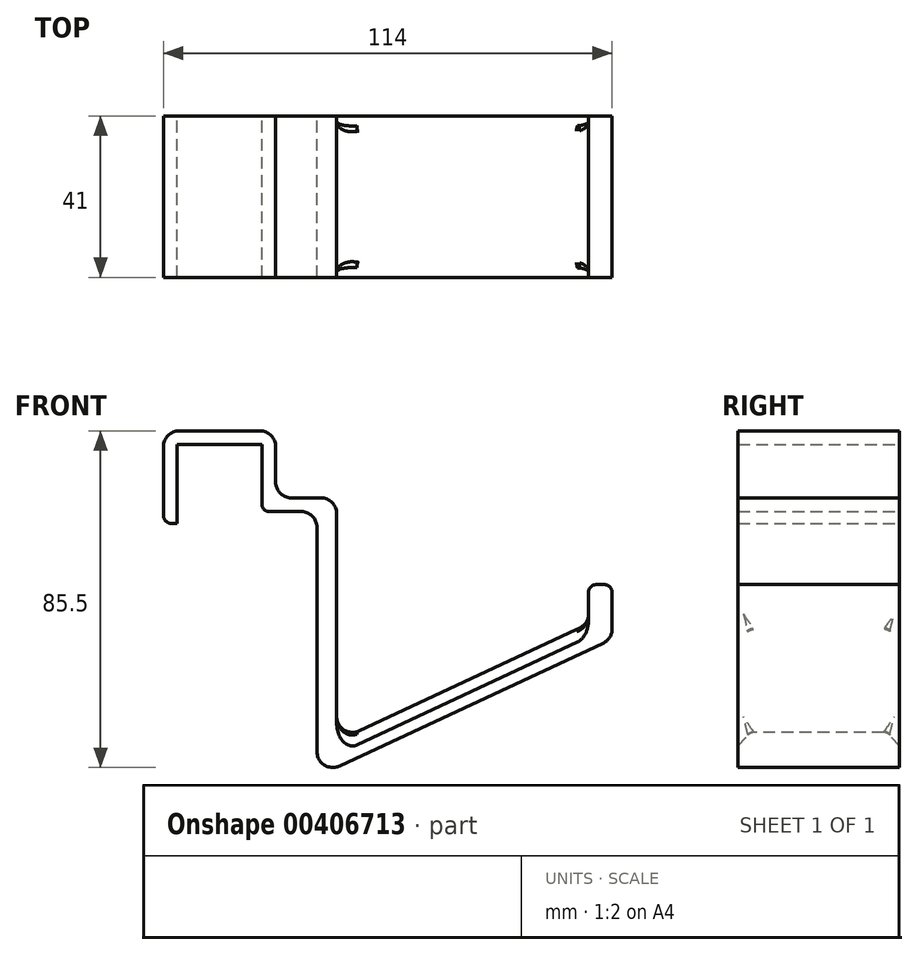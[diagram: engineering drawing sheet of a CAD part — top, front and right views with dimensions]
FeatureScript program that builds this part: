
annotation { "Feature Type Name" : "Feature", "Feature Type Description" : "" }
export const myFeature = defineFeature(function(context is Context, id is Id, definition is map)
    precondition{}
    {
        {
            var Q0;
            Q0=qCreatedBy(makeId("Front.planeOp"),FACE);
            var sketch = newSketch(context, id + "F0", { "sketchPlane" : qUnion([Q0])});
            skLineSegment(sketch, "E0", {"start": v(-40.5, 62) * mm, "end": v(-40.5, 82) * mm});
            skLineSegment(sketch, "E1", {"start": v(-40.5, 82) * mm, "end": v(-19, 82) * mm});
            skLineSegment(sketch, "E2", {"start": v(-19, 82) * mm, "end": v(-19, 65) * mm});
            skLineSegment(sketch, "E3", {"start": v(-19, 65) * mm, "end": v(-5, 65) * mm});
            skLineSegment(sketch, "E4", {"start": v(-5, 65) * mm, "end": v(-5, 0) * mm});
            skLineSegment(sketch, "E5.4", {"start": v(-44, 62) * mm, "end": v(-44, 85.5) * mm});
            skLineSegment(sketch, "E5.5", {"start": v(-44, 85.5) * mm, "end": v(-15.5, 85.5) * mm});
            skLineSegment(sketch, "E5.6", {"start": v(-15.5, 85.5) * mm, "end": v(-15.5, 68.5) * mm});
            skLineSegment(sketch, "E5.7", {"start": v(-15.5, 68.5) * mm, "end": v(0, 68.5) * mm});
            skLineSegment(sketch, "E6", {"start": v(-44, 62) * mm, "end": v(-40.5, 62) * mm});
            skLineSegment(sketch, "E7", {"start": v(0, 0) * mm, "end": v(0, 0) * mm});
            skLineSegment(sketch, "E8", {"start": v(0, 0) * mm, "end": v(-5, 0) * mm});
            skLineSegment(sketch, "E9", {"start": v(0, 68.5) * mm, "end": v(0, 6.62) * mm});
            skLineSegment(sketch, "E10", {"start": v(0, 6.62) * mm, "end": v(64, 36.46) * mm});
            skLineSegment(sketch, "E11", {"start": v(64, 36.46) * mm, "end": v(64, 46.46) * mm});
            skLineSegment(sketch, "E12", {"start": v(64, 46.46) * mm, "end": v(70, 46.46) * mm});
            skLineSegment(sketch, "E13", {"start": v(70, 46.46) * mm, "end": v(70, 32.64) * mm});
            skLineSegment(sketch, "E14", {"start": v(70, 32.64) * mm, "end": v(0, 0) * mm});
            skSolve(sketch);
        }
        {
            var Q0;
            Q0=makeQuery(id+"F0.imprint","IMPRINT",FACE,{"disambiguationData":[TD([[makeQuery(id+"F0.imprint","IMPRINT",EDGE,{"derivedFrom":sQuery(id+"F0.wireOp",EDGE,"E0")}),1.0]])]});
            var Q1;
            {var subQ1=sQuery(id+"F0.wireOp",EDGE,"AhkrgUPT-9Wn4-kyPp-FIpI-RrMK1532yphD");Q1=makeQuery(id+"F0.imprint","IMPRINT",FACE,{"disambiguationData":[TD([[makeQuery(id+"F0.imprint","IMPRINT",EDGE,{"derivedFrom":subQ1}),1.0]])]});}
            extrude(context, id + "F1", {"entities" : qUnion([Q0, Q1]), "depth" : 41 * mm});
        }
        {
            var Q0;
            Q0=makeQuery(id+"F1.opExtrude","CAP_EDGE",EDGE,{"disambiguationData":[OSD([sQuery(id+"F0.wireOp",EDGE,"E10")])],"isStart":true});
            var Q1;
            Q1=makeQuery(id+"F1.opExtrude","CAP_EDGE",EDGE,{"disambiguationData":[OSD([sQuery(id+"F0.wireOp",EDGE,"E10")])],"isStart":false});
            chamfer(context, id + "F2", {"entities" : qUnion([Q0, Q1]), "width" : 3 * mm, "tangentPropagation" : true});
        }
        {
            var Q0;
            Q0=makeQuery(id+"F1.opExtrude","SWEPT_EDGE",EDGE,{"disambiguationData":[OSD([sQuery(id+"F0.wireOp",EDGE,"E5.4"),sQuery(id+"F0.wireOp",EDGE,"E5.5")])]});
            var Q1;
            Q1=makeQuery(id+"F1.opExtrude","SWEPT_EDGE",EDGE,{"disambiguationData":[OSD([sQuery(id+"F0.wireOp",EDGE,"E5.5"),sQuery(id+"F0.wireOp",EDGE,"E5.6")])]});
            var Q2;
            Q2=makeQuery(id+"F1.opExtrude","SWEPT_EDGE",EDGE,{"disambiguationData":[OSD([sQuery(id+"F0.wireOp",EDGE,"E5.3"),sQuery(id+"F0.wireOp",EDGE,"E5.7")])]});
            var Q3;
            Q3=makeQuery(id+"F1.opExtrude","SWEPT_EDGE",EDGE,{"disambiguationData":[OSD([sQuery(id+"F0.wireOp",EDGE,"E5.2"),sQuery(id+"F0.wireOp",EDGE,"E5.3"),sQuery(id+"F0.wireOp",EDGE,"E7")])]});
            var Q4;
            Q4=makeQuery(id+"F1.opExtrude","SWEPT_EDGE",EDGE,{"disambiguationData":[OSD([sQuery(id+"F0.wireOp",EDGE,"E5.6"),sQuery(id+"F0.wireOp",EDGE,"E5.7")])]});
            var Q5;
            Q5=makeQuery(id+"F1.opExtrude","SWEPT_EDGE",EDGE,{"disambiguationData":[OSD([sQuery(id+"F0.wireOp",EDGE,"E5.1"),sQuery(id+"F0.wireOp",EDGE,"E5.2")])]});
            var Q6;
            Q6=makeQuery(id+"F1.opExtrude","SWEPT_EDGE",EDGE,{"disambiguationData":[OSD([sQuery(id+"F0.wireOp",EDGE,"E5.0"),sQuery(id+"F0.wireOp",EDGE,"E5.1")])]});
            var Q7;
            Q7=makeQuery(id+"F1.opExtrude","SWEPT_EDGE",EDGE,{"disambiguationData":[OSD([sQuery(id+"F0.wireOp",EDGE,"E4"),sQuery(id+"F0.wireOp",EDGE,"RCLY0lTh-qNke-Zs5P-apW9-nbSzTQWvxzDQ")])]});
            var Q8;
            Q8=makeQuery(id+"F1.opExtrude","SWEPT_EDGE",EDGE,{"disambiguationData":[OSD([sQuery(id+"F0.wireOp",EDGE,"E9"),sQuery(id+"F0.wireOp",EDGE,"E10")])]});
            var Q9;
            Q9=makeQuery(id+"F1.opExtrude","SWEPT_EDGE",EDGE,{"disambiguationData":[OSD([sQuery(id+"F0.wireOp",EDGE,"E10"),sQuery(id+"F0.wireOp",EDGE,"E11")])]});
            var Q10;
            Q10=makeQuery(id+"F1.opExtrude","SWEPT_EDGE",EDGE,{"disambiguationData":[OSD([sQuery(id+"F0.wireOp",EDGE,"E13"),sQuery(id+"F0.wireOp",EDGE,"E14")])]});
            var Q11;
            Q11=makeQuery(id+"F1.opExtrude","SWEPT_EDGE",EDGE,{"disambiguationData":[OSD([sQuery(id+"F0.wireOp",EDGE,"E8"),sQuery(id+"F0.wireOp",EDGE,"E14")])]});
            var Q12;
            Q12=makeQuery(id+"F2.opChamfer","BLEND_EDGE",EDGE,{"blendedFrom":[makeQuery(id+"F1.opExtrude","CAP_EDGE",EDGE,{"disambiguationData":[OSD([sQuery(id+"F0.wireOp",EDGE,"E10")])],"isStart":false}),makeQuery(id+"F1.opExtrude","SWEPT_FACE",FACE,{"disambiguationData":[OSD([sQuery(id+"F0.wireOp",EDGE,"E9")])]})],"blendedInto":[makeQuery(id+"F1.opExtrude","SWEPT_FACE",FACE,{"disambiguationData":[OSD([sQuery(id+"F0.wireOp",EDGE,"E9")])]})]});
            var Q13;
            Q13=makeQuery(id+"F2.opChamfer","BLEND_EDGE",EDGE,{"blendedFrom":[makeQuery(id+"F1.opExtrude","CAP_EDGE",EDGE,{"disambiguationData":[OSD([sQuery(id+"F0.wireOp",EDGE,"E10")])],"isStart":true}),makeQuery(id+"F1.opExtrude","SWEPT_FACE",FACE,{"disambiguationData":[OSD([sQuery(id+"F0.wireOp",EDGE,"E9")])]})],"blendedInto":[makeQuery(id+"F1.opExtrude","SWEPT_FACE",FACE,{"disambiguationData":[OSD([sQuery(id+"F0.wireOp",EDGE,"E9")])]})]});
            var Q14;
            Q14=makeQuery(id+"F2.opChamfer","BLEND_EDGE",EDGE,{"blendedFrom":[makeQuery(id+"F1.opExtrude","CAP_EDGE",EDGE,{"disambiguationData":[OSD([sQuery(id+"F0.wireOp",EDGE,"E10")])],"isStart":false}),makeQuery(id+"F1.opExtrude","SWEPT_FACE",FACE,{"disambiguationData":[OSD([sQuery(id+"F0.wireOp",EDGE,"E11")])]})],"blendedInto":[makeQuery(id+"F1.opExtrude","SWEPT_FACE",FACE,{"disambiguationData":[OSD([sQuery(id+"F0.wireOp",EDGE,"E11")])]})]});
            var Q15;
            Q15=makeQuery(id+"F2.opChamfer","BLEND_EDGE",EDGE,{"blendedFrom":[makeQuery(id+"F1.opExtrude","CAP_EDGE",EDGE,{"disambiguationData":[OSD([sQuery(id+"F0.wireOp",EDGE,"E10")])],"isStart":true}),makeQuery(id+"F1.opExtrude","SWEPT_FACE",FACE,{"disambiguationData":[OSD([sQuery(id+"F0.wireOp",EDGE,"E11")])]})],"blendedInto":[makeQuery(id+"F1.opExtrude","SWEPT_FACE",FACE,{"disambiguationData":[OSD([sQuery(id+"F0.wireOp",EDGE,"E11")])]})]});
            fillet(context, id + "F3", {"entities" : qUnion([Q0, Q1, Q2, Q3, Q4, Q5, Q6, Q7, Q8, Q9, Q10, Q11, Q12, Q13, Q14, Q15]), "radius" : 4 * mm, "tangentPropagation" : true, "allowEdgeOverflow" : false});
        }
        {
            var Q0;
            Q0=makeQuery(id+"F1.opExtrude","SWEPT_EDGE",EDGE,{"disambiguationData":[OSD([sQuery(id+"F0.wireOp",EDGE,"E5.4"),sQuery(id+"F0.wireOp",EDGE,"E6")])]});
            var Q1;
            Q1=makeQuery(id+"F1.opExtrude","SWEPT_EDGE",EDGE,{"disambiguationData":[OSD([sQuery(id+"F0.wireOp",EDGE,"HffoBBfD-ZpNb-Def4-HJbs-I6yT36w8jhyF"),sQuery(id+"F0.wireOp",EDGE,"Ouw1DOu0-Xpgy-L17c-oILG-WZkcb7lERYxI")])]});
            var Q2;
            Q2=makeQuery(id+"F1.opExtrude","SWEPT_EDGE",EDGE,{"disambiguationData":[OSD([sQuery(id+"F0.wireOp",EDGE,"E5.0"),sQuery(id+"F0.wireOp",EDGE,"Ouw1DOu0-Xpgy-L17c-oILG-WZkcb7lERYxI")])]});
            var Q3;
            Q3=makeQuery(id+"F1.opExtrude","SWEPT_EDGE",EDGE,{"disambiguationData":[OSD([sQuery(id+"F0.wireOp",EDGE,"E2"),sQuery(id+"F0.wireOp",EDGE,"E3")])]});
            var Q4;
            Q4=makeQuery(id+"F1.opExtrude","SWEPT_EDGE",EDGE,{"disambiguationData":[OSD([sQuery(id+"F0.wireOp",EDGE,"E11"),sQuery(id+"F0.wireOp",EDGE,"E12")])]});
            var Q5;
            Q5=makeQuery(id+"F1.opExtrude","SWEPT_EDGE",EDGE,{"disambiguationData":[OSD([sQuery(id+"F0.wireOp",EDGE,"E12"),sQuery(id+"F0.wireOp",EDGE,"E13")])]});
            var Q6;
            {var subQ0=sQuery(id+"F0.wireOp",EDGE,"E10");Q6=makeQuery(id+"F2.opChamfer","BLEND_EDGE",EDGE,{"blendedFrom":[makeQuery(id+"F1.opExtrude","CAP_EDGE",EDGE,{"disambiguationData":[OSD([subQ0])],"isStart":false}),makeQuery(id+"F1.opExtrude","SWEPT_FACE",FACE,{"disambiguationData":[OSD([subQ0])]})],"blendedInto":[makeQuery(id+"F1.opExtrude","SWEPT_FACE",FACE,{"disambiguationData":[OSD([subQ0])]})]});}
            var Q7;
            {var subQ0=sQuery(id+"F0.wireOp",EDGE,"E10");Q7=makeQuery(id+"F2.opChamfer","BLEND_EDGE",EDGE,{"blendedFrom":[makeQuery(id+"F1.opExtrude","CAP_EDGE",EDGE,{"disambiguationData":[OSD([subQ0])],"isStart":true}),makeQuery(id+"F1.opExtrude","SWEPT_FACE",FACE,{"disambiguationData":[OSD([subQ0])]})],"blendedInto":[makeQuery(id+"F1.opExtrude","SWEPT_FACE",FACE,{"disambiguationData":[OSD([subQ0])]})]});}
            fillet(context, id + "F4", {"entities" : qUnion([Q0, Q1, Q2, Q3, Q4, Q5, Q6, Q7]), "radius" : 2 * mm, "tangentPropagation" : true, "allowEdgeOverflow" : false});
        }
    });
